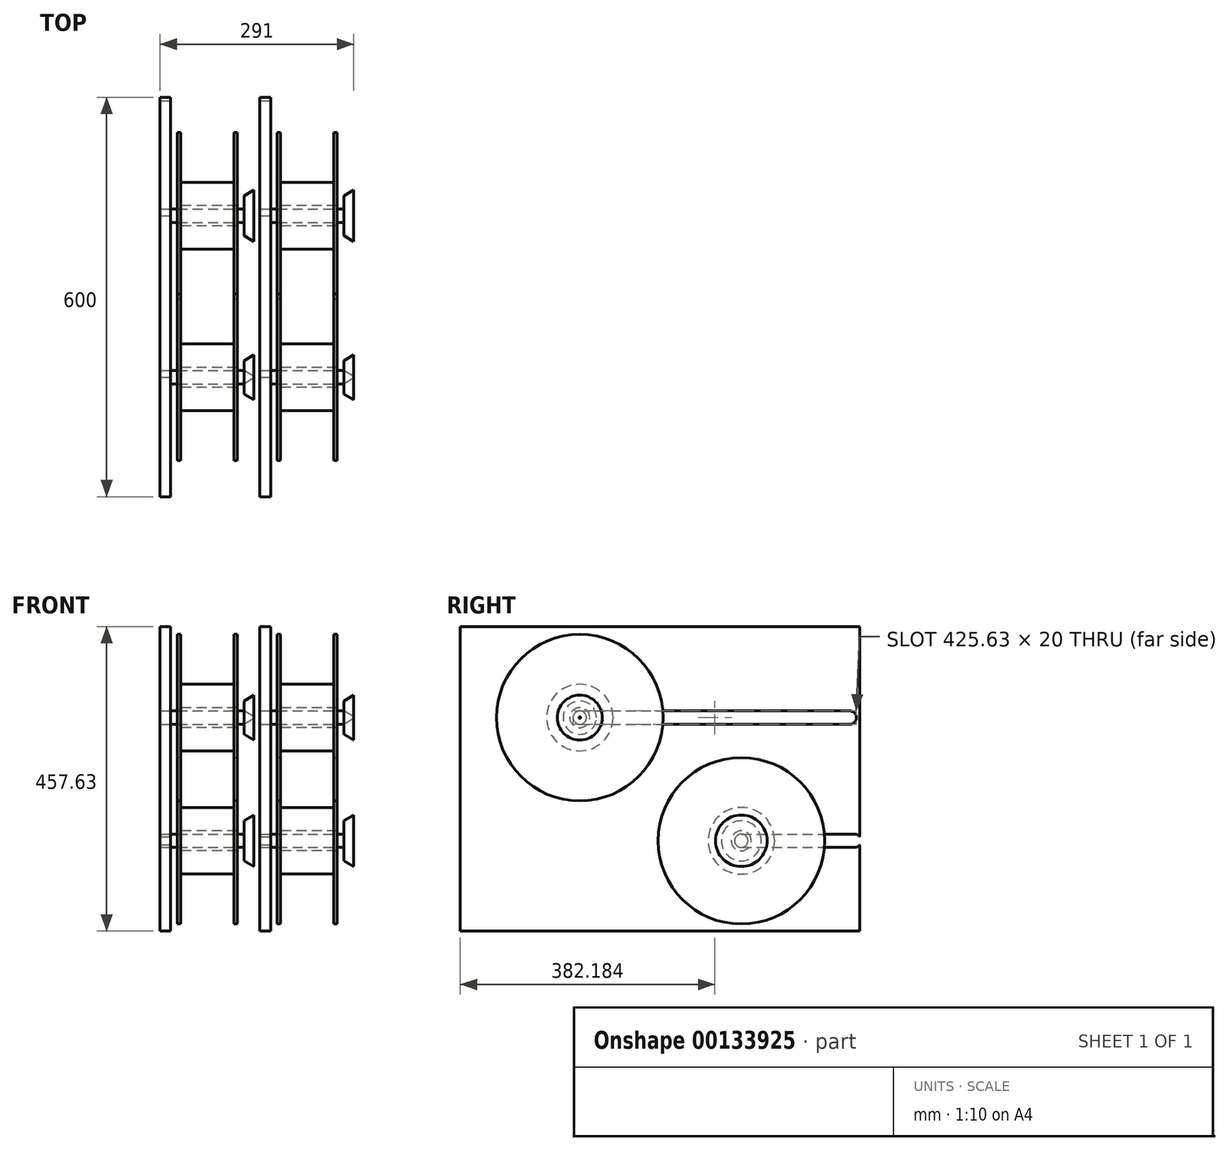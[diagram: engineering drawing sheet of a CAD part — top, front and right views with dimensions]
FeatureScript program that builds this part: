
annotation { "Feature Type Name" : "Feature", "Feature Type Description" : "" }
export const myFeature = defineFeature(function(context is Context, id is Id, definition is map)
    precondition{}
    {
        {
            var Q0;
            Q0=qCreatedBy(makeId("Right.planeOp"),FACE);
            var sketch = newSketch(context, id + "F0", { "sketchPlane" : qUnion([Q0])});
            skLineSegment(sketch, "E0.bottom", {"start": v(0, 0) * mm, "end": v(-600, 0) * mm});
            skLineSegment(sketch, "E0.top", {"start": v(0, 457.63) * mm, "end": v(-600, 457.63) * mm});
            skLineSegment(sketch, "E0.left", {"start": v(0, 0) * mm, "end": v(0, 457.63) * mm});
            skLineSegment(sketch, "E0.right", {"start": v(-600, 0) * mm, "end": v(-600, 457.63) * mm});
            skCircle(sketch, "E1", {"center": v(-420.63, 320.82) * mm, "radius": 125 * mm});
            skLineSegment(sketch, "E2", {"start": v(-600, 457.63) * mm, "end": v(0, 0) * mm, "construction": true});
            skLineSegment(sketch, "E3.bottom", {"start": v(-420.63, 320.82) * mm, "end": v(-600, 320.82) * mm, "construction": true});
            skLineSegment(sketch, "E3.top", {"start": v(-420.63, 457.63) * mm, "end": v(-600, 457.63) * mm, "construction": true});
            skLineSegment(sketch, "E3.left", {"start": v(-420.63, 320.82) * mm, "end": v(-420.63, 457.63) * mm, "construction": true});
            skLineSegment(sketch, "E3.right", {"start": v(-600, 320.82) * mm, "end": v(-600, 457.63) * mm, "construction": true});
            skLineSegment(sketch, "E4.bottom", {"start": v(0, 0) * mm, "end": v(-178.02, 0) * mm, "construction": true});
            skLineSegment(sketch, "E4.top", {"start": v(0, 135.78) * mm, "end": v(-178.02, 135.78) * mm, "construction": true});
            skLineSegment(sketch, "E4.left", {"start": v(0, 0) * mm, "end": v(0, 135.78) * mm, "construction": true});
            skLineSegment(sketch, "E4.right", {"start": v(-178.02, 0) * mm, "end": v(-178.02, 135.78) * mm, "construction": true});
            skCircle(sketch, "E5", {"center": v(-178.02, 135.78) * mm, "radius": 125 * mm});
            skCircle(sketch, "E6", {"center": v(-420.63, 320.82) * mm, "radius": 50 * mm});
            skCircle(sketch, "E7", {"center": v(-178.02, 135.78) * mm, "radius": 50 * mm});
            skCircle(sketch, "E8", {"center": v(-178.02, 135.78) * mm, "radius": 15 * mm});
            skCircle(sketch, "E9", {"center": v(-420.63, 320.82) * mm, "radius": 15 * mm});
            skSolve(sketch);
        }
        {
            var Q0;
            Q0=makeQuery(id+"F0.imprint","IMPRINT",FACE,{"disambiguationData":[TD([[makeQuery(id+"F0.imprint","IMPRINT",EDGE,{"derivedFrom":sQuery(id+"F0.wireOp",EDGE,"E1")}),1.0]])]});
            var Q1;
            Q1=makeQuery(id+"F0.imprint","IMPRINT",FACE,{"disambiguationData":[TD([[makeQuery(id+"F0.imprint","IMPRINT",EDGE,{"derivedFrom":sQuery(id+"F0.wireOp",EDGE,"E6")}),1.0]])]});
            var Q2;
            Q2=makeQuery(id+"F0.imprint","IMPRINT",FACE,{"disambiguationData":[TD([[makeQuery(id+"F0.imprint","IMPRINT",EDGE,{"derivedFrom":sQuery(id+"F0.wireOp",EDGE,"E7")}),1.0]])]});
            var Q3;
            Q3=makeQuery(id+"F0.imprint","IMPRINT",FACE,{"disambiguationData":[TD([[makeQuery(id+"F0.imprint","IMPRINT",EDGE,{"derivedFrom":sQuery(id+"F0.wireOp",EDGE,"E5")}),1.0]])]});
            extrude(context, id + "F1", {"entities" : qUnion([Q0, Q1, Q2, Q3]), "depth" : 5 * mm});
        }
        {
            var Q0;
            Q0=makeQuery(id+"F0.imprint","IMPRINT",FACE,{"disambiguationData":[TD([[makeQuery(id+"F0.imprint","IMPRINT",EDGE,{"derivedFrom":sQuery(id+"F0.wireOp",EDGE,"E6")}),1.0]])]});
            var Q1;
            Q1=makeQuery(id+"F0.imprint","IMPRINT",FACE,{"disambiguationData":[TD([[makeQuery(id+"F0.imprint","IMPRINT",EDGE,{"derivedFrom":sQuery(id+"F0.wireOp",EDGE,"E7")}),1.0]])]});
            extrude(context, id + "F2", {"entities" : qUnion([Q0, Q1]), "operationType" : NewBodyOperationType.ADD, "depth" : 90 * mm});
        }
        {
            var Q0;
            Q0=makeQuery(id+"F2.opExtrude","CAP_FACE",FACE,{"disambiguationData":[OSD([sQuery(id+"F0.wireOp",EDGE,"E6")])],"isStart":false});
            var sketch = newSketch(context, id + "F3", { "sketchPlane" : qUnion([Q0])});
            skCircle(sketch, "E10", {"center": v(-420.63, 320.82) * mm, "radius": 125 * mm});
            skCircle(sketch, "E11", {"center": v(-178.02, 135.78) * mm, "radius": 125 * mm});
            skCircle(sketch, "E12", {"center": v(-178.02, 135.78) * mm, "radius": 15 * mm});
            skSolve(sketch);
        }
        {
            var Q0;
            Q0=makeQuery(id+"F3.imprint","IMPRINT",FACE,{"disambiguationData":[TD([[makeQuery(id+"F3.imprint","IMPRINT",EDGE,{"derivedFrom":sQuery(id+"F3.wireOp",EDGE,"E10")}),1.0]])]});
            var Q1;
            Q1=makeQuery(id+"F3.imprint","IMPRINT",FACE,{"disambiguationData":[TD([[makeQuery(id+"F3.imprint","IMPRINT",EDGE,{"derivedFrom":sQuery(id+"F3.wireOp",EDGE,"E11")}),1.0]])]});
            extrude(context, id + "F4", {"entities" : qUnion([Q0, Q1]), "operationType" : NewBodyOperationType.ADD, "oppositeDirection" : true, "depth" : 5 * mm});
        }
        {
            var Q0;
            Q0=qCreatedBy(makeId("Right.planeOp"),FACE);
            cPlane(context, id + "F5", {"entities" : qUnion([Q0]), "cplaneType" : CPlaneType.OFFSET, "offset" : 10 * mm, "oppositeDirection" : true, "width" : 150 * mm, "height" : 150 * mm});
        }
        {
            var Q0;
            Q0=qCreatedBy(id+"F5.planeOp",FACE);
            var sketch = newSketch(context, id + "F6", { "sketchPlane" : qUnion([Q0])});
            skCircle(sketch, "E13", {"center": v(-178.02, 135.78) * mm, "radius": 10 * mm});
            skCircle(sketch, "E14", {"center": v(-420.63, 320.82) * mm, "radius": 10 * mm});
            skLineSegment(sketch, "E15.bottom", {"start": v(0, 0) * mm, "end": v(-600, 0) * mm});
            skLineSegment(sketch, "E15.top", {"start": v(0, 457.63) * mm, "end": v(-600, 457.63) * mm});
            skLineSegment(sketch, "E15.left", {"start": v(0, 0) * mm, "end": v(0, 457.63) * mm});
            skLineSegment(sketch, "E15.right", {"start": v(-600, 0) * mm, "end": v(-600, 457.63) * mm});
            skLineSegment(sketch, "E16", {"start": v(-178.02, 135.78) * mm, "end": v(-8.02, 135.78) * mm, "construction": true});
            skLineSegment(sketch, "E17", {"start": v(-420.63, 320.82) * mm, "end": v(-15, 320.82) * mm, "construction": true});
            skArc(sketch, "E18.0.startCap", {"start": v(-420.63, 310.82) * mm, "mid": v(-430.63, 320.82) * mm, "end": v(-420.63, 330.82) * mm});
            skArc(sketch, "E18.0.endCap", {"start": v(-15, 330.82) * mm, "mid": v(-5, 320.82) * mm, "end": v(-15, 310.82) * mm});
            skLineSegment(sketch, "E18.0.left", {"start": v(-420.63, 330.82) * mm, "end": v(-15, 330.82) * mm});
            skLineSegment(sketch, "E18.0.right", {"start": v(-420.63, 310.82) * mm, "end": v(-15, 310.82) * mm});
            skArc(sketch, "E19.0.startCap", {"start": v(-178.02, 125.78) * mm, "mid": v(-188.02, 135.78) * mm, "end": v(-178.02, 145.78) * mm});
            skArc(sketch, "E19.0.endCap", {"start": v(-8.02, 145.78) * mm, "mid": v(1.98, 135.78) * mm, "end": v(-8.02, 125.78) * mm});
            skLineSegment(sketch, "E19.0.left", {"start": v(-178.02, 145.78) * mm, "end": v(-8.02, 145.78) * mm});
            skLineSegment(sketch, "E19.0.right", {"start": v(-178.02, 125.78) * mm, "end": v(-8.02, 125.78) * mm});
            skSolve(sketch);
        }
        {
            var Q0;
            Q0=makeQuery(id+"F6.imprint","IMPRINT",FACE,{"disambiguationData":[TD([[makeQuery(id+"F6.imprint","IMPRINT",EDGE,{"derivedFrom":sQuery(id+"F6.wireOp",EDGE,"E13")}),1.0]])]});
            var Q1;
            Q1=makeQuery(id+"F6.imprint","IMPRINT",FACE,{"disambiguationData":[TD([[makeQuery(id+"F6.imprint","IMPRINT",EDGE,{"derivedFrom":sQuery(id+"F6.wireOp",EDGE,"E14")}),1.0]])]});
            var Q2;
            {var subQ2=sQuery(id+"F6.wireOp",EDGE,"E15.bottom");Q2=makeQuery(id+"F6.imprint","IMPRINT",FACE,{"disambiguationData":[TD([[makeQuery(id+"F6.imprint","IMPRINT",EDGE,{"derivedFrom":subQ2}),-1.0]])]});}
            extrude(context, id + "F7", {"entities" : qUnion([Q0, Q1, Q2]), "oppositeDirection" : true, "depth" : 16 * mm});
        }
        {
            var Q0;
            Q0=makeQuery(id+"F6.imprint","IMPRINT",FACE,{"disambiguationData":[TD([[makeQuery(id+"F6.imprint","IMPRINT",EDGE,{"derivedFrom":sQuery(id+"F6.wireOp",EDGE,"E13")}),1.0]])]});
            var Q1;
            Q1=makeQuery(id+"F6.imprint","IMPRINT",FACE,{"disambiguationData":[TD([[makeQuery(id+"F6.imprint","IMPRINT",EDGE,{"derivedFrom":sQuery(id+"F6.wireOp",EDGE,"E14")}),1.0]])]});
            extrude(context, id + "F8", {"entities" : qUnion([Q0, Q1]), "operationType" : NewBodyOperationType.ADD, "depth" : 110 * mm});
        }
        {
            var Q0;
            Q0=makeQuery(id+"F8.opExtrude","CAP_FACE",FACE,{"disambiguationData":[OSD([sQuery(id+"F6.wireOp",EDGE,"E14")])],"isStart":false});
            var sketch = newSketch(context, id + "F9", { "sketchPlane" : qUnion([Q0])});
            skCircle(sketch, "E20", {"center": v(-178.02, 135.78) * mm, "radius": 30 * mm});
            skCircle(sketch, "E21", {"center": v(-420.63, 320.82) * mm, "radius": 25 * mm});
            skSolve(sketch);
        }
        {
            var Q0;
            Q0=makeQuery(id+"F9.imprint","IMPRINT",FACE,{"disambiguationData":[TD([[makeQuery(id+"F9.imprint","IMPRINT",EDGE,{"derivedFrom":sQuery(id+"F9.wireOp",EDGE,"E20")}),1.0]])]});
            var Q1;
            Q1=makeQuery(id+"F9.imprint","IMPRINT",FACE,{"disambiguationData":[TD([[makeQuery(id+"F9.imprint","IMPRINT",EDGE,{"derivedFrom":sQuery(id+"F9.wireOp",EDGE,"E21")}),1.0]])]});
            extrude(context, id + "F10", {"entities" : qUnion([Q0, Q1]), "depth" : 15 * mm, "hasDraft" : true, "draftAngle" : 30 * degree});
        }
        {
            var Q0;
            Q0=makeQuery(id+"F10.opExtrude","SWEPT_BODY",BODY,{"disambiguationData":[OSD([sQuery(id+"F6.wireOp",EDGE,"E14"),sQuery(id+"F9.wireOp",EDGE,"E21")])]});
            var Q1;
            Q1=makeQuery(id+"F10.opExtrude","SWEPT_BODY",BODY,{"disambiguationData":[OSD([sQuery(id+"F9.wireOp",EDGE,"E20")])]});
            var Q2;
            Q2=makeQuery(id+"F7.opExtrude","SWEPT_BODY",BODY,{"disambiguationData":[OSD([sQuery(id+"F6.wireOp",EDGE,"E13"),sQuery(id+"F6.wireOp",EDGE,"E14"),sQuery(id+"F6.wireOp",EDGE,"E15.bottom"),sQuery(id+"F6.wireOp",EDGE,"E15.top"),sQuery(id+"F6.wireOp",EDGE,"E15.left"),sQuery(id+"F6.wireOp",EDGE,"E15.right"),sQuery(id+"F6.wireOp",EDGE,"E18.0.endCap"),sQuery(id+"F6.wireOp",EDGE,"E18.0.left"),sQuery(id+"F6.wireOp",EDGE,"E18.0.right"),sQuery(id+"F6.wireOp",EDGE,"E19.0.endCap"),sQuery(id+"F6.wireOp",EDGE,"E19.0.left"),sQuery(id+"F6.wireOp",EDGE,"E19.0.right")])]});
            var Q3;
            Q3=makeQuery(id+"F1.opExtrude","SWEPT_BODY",BODY,{"disambiguationData":[OSD([sQuery(id+"F0.wireOp",EDGE,"E5"),sQuery(id+"F0.wireOp",EDGE,"E8")])]});
            var Q4;
            Q4=makeQuery(id+"F1.opExtrude","SWEPT_BODY",BODY,{"disambiguationData":[OSD([sQuery(id+"F0.wireOp",EDGE,"E1"),sQuery(id+"F0.wireOp",EDGE,"E9")])]});
            transform(context, id + "F11", {"entities" : qUnion([Q0, Q1, Q2, Q3, Q4]), "transformType" : TransformType.TRANSLATION_3D, "dx" : 150 * mm, "dy" : 0 * mm, "dz" : 0 * mm, "makeCopy" : true});
        }
    });
